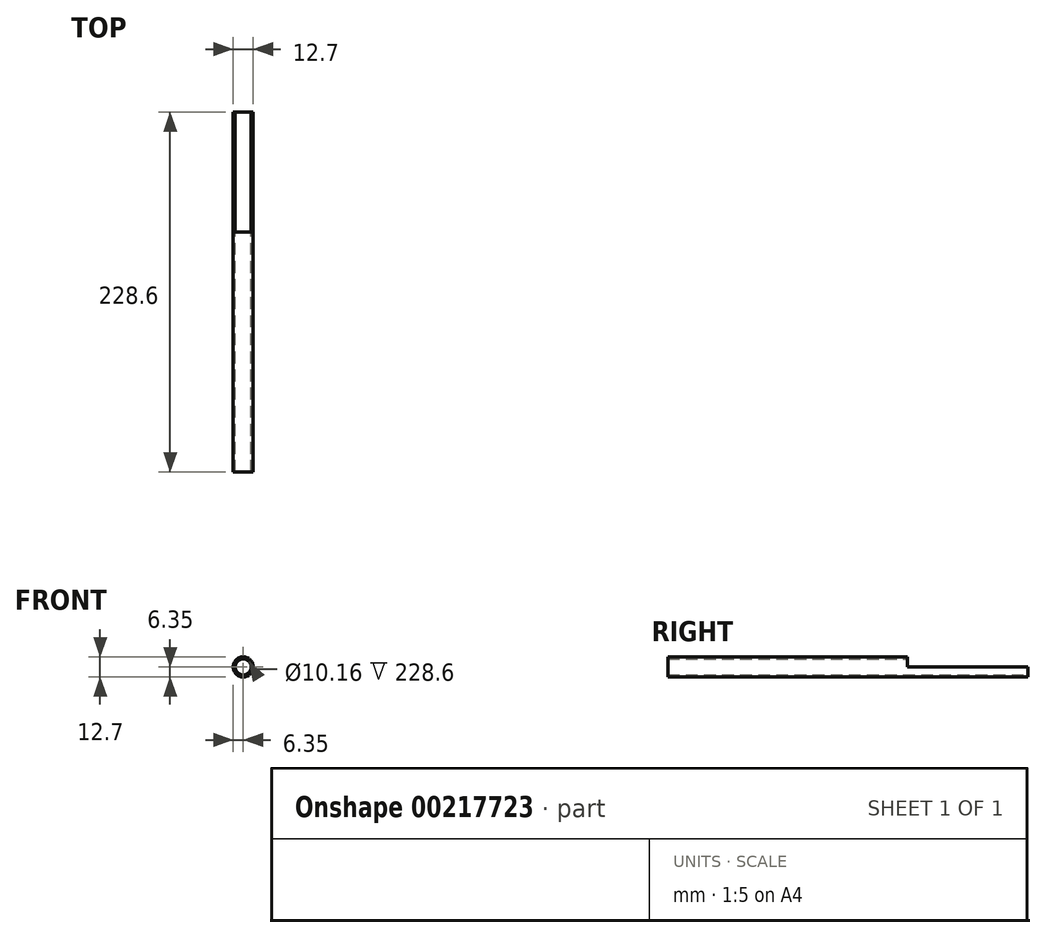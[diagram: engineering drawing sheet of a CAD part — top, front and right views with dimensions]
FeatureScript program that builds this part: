
annotation { "Feature Type Name" : "Feature", "Feature Type Description" : "" }
export const myFeature = defineFeature(function(context is Context, id is Id, definition is map)
    precondition{}
    {
        {
            var Q0;
            Q0=qCreatedBy(makeId("Front.planeOp"),FACE);
            var sketch = newSketch(context, id + "F0", { "sketchPlane" : qUnion([Q0])});
            skCircle(sketch, "E0", {"center": v(0, 0) * mm, "radius": 6.35 * mm});
            skCircle(sketch, "E1", {"center": v(0, 0) * mm, "radius": 5.08 * mm});
            skLineSegment(sketch, "E2.trimOffspring", {"start": v(5.08, 0) * mm, "end": v(6.35, 0) * mm});
            skPoint(sketch, "E3.start.orphan", {"position": v(-6.35, 0) * mm});
            skLineSegment(sketch, "E4", {"start": v(-6.35, 0) * mm, "end": v(-5.08, 0) * mm});
            skSolve(sketch);
        }
        {
            var Q0;
            Q0 = qSketchRegion(id + "F0", true);
            extrude(context, id + "F1", {"entities" : qUnion([Q0]), "depth" : 152.4 * mm, "offsetDistance" : 25.4 * mm});
        }
        {
            var Q0;
            {var subQ0=sQuery(id+"F0.wireOp",EDGE,"E2.trimOffspring");Q0=makeQuery(id+"F0.imprint","IMPRINT",FACE,{"disambiguationData":[TD([[makeQuery(id+"F0.imprint","IMPRINT",EDGE,{"derivedFrom":subQ0}),-1.0]])]});}
            extrude(context, id + "F2", {"entities" : qUnion([Q0]), "operationType" : NewBodyOperationType.ADD, "oppositeDirection" : true, "depth" : 76.2 * mm, "offsetDistance" : 25.4 * mm});
        }
    });
